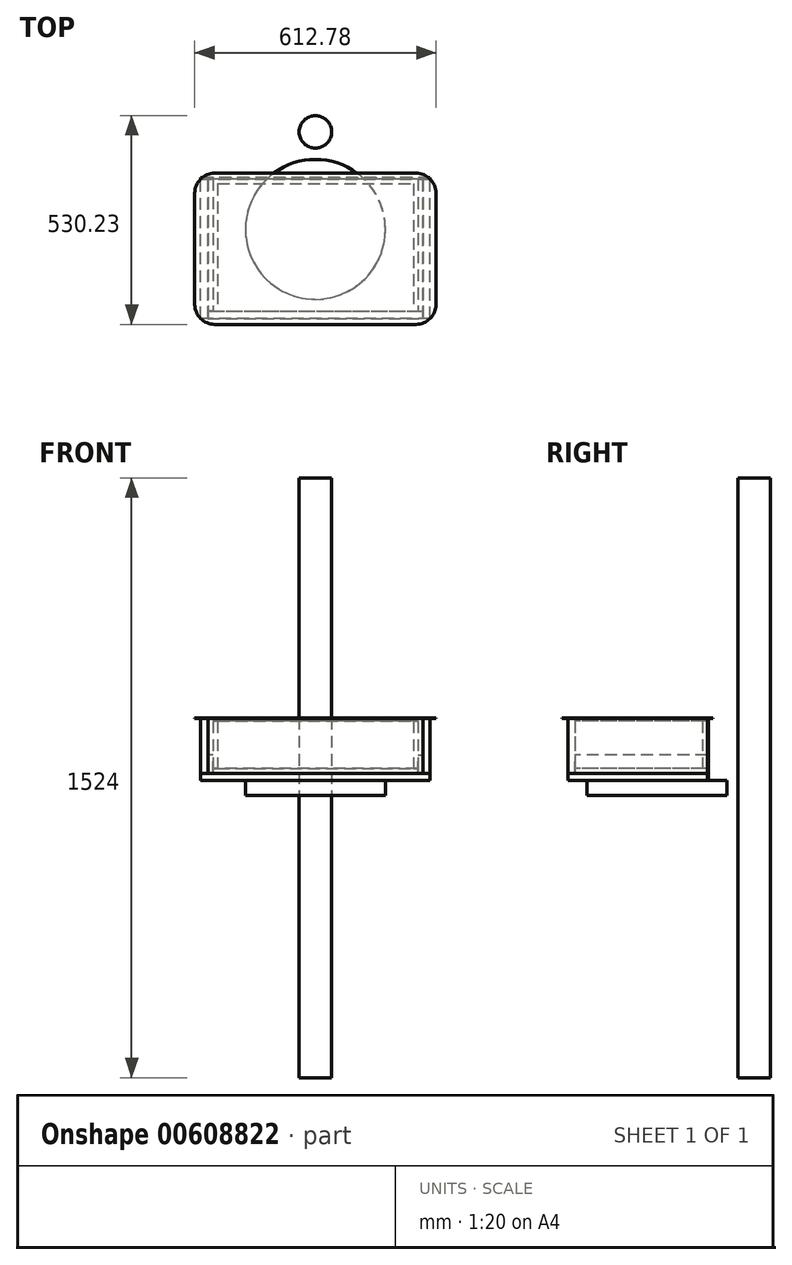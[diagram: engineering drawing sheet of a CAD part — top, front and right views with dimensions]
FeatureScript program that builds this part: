
annotation { "Feature Type Name" : "Feature", "Feature Type Description" : "" }
export const myFeature = defineFeature(function(context is Context, id is Id, definition is map)
    precondition{}
    {
        {
            var Q0;
            Q0=qCreatedBy(makeId("Top.planeOp"),FACE);
            var sketch = newSketch(context, id + "F0", { "sketchPlane" : qUnion([Q0])});
            skCircle(sketch, "E0", {"center": v(0, 0) * mm, "radius": 177.8 * mm});
            skSolve(sketch);
        }
        {
            var Q0;
            Q0 = qSketchRegion(id + "F0", true);
            extrude(context, id + "F1", {"entities" : qUnion([Q0]), "depth" : 38.1 * mm, "offsetDistance" : 25.4 * mm});
        }
        {
            var Q0;
            Q0=makeQuery(id+"F1.opExtrude","CAP_FACE",FACE,{"disambiguationData":[OSD([sQuery(id+"F0.wireOp",EDGE,"E0")])],"isStart":false});
            cPlane(context, id + "F2", {"entities" : qUnion([Q0]), "cplaneType" : CPlaneType.OFFSET, "offset" : 157.96 * mm, "width" : 152.4 * mm, "height" : 152.4 * mm});
        }
        {
            var Q0;
            Q0=qCreatedBy(id+"F2.planeOp",FACE);
            var sketch = newSketch(context, id + "F3", { "sketchPlane" : qUnion([Q0])});
            skLineSegment(sketch, "E1.bottom", {"start": v(255.59, -241.3) * mm, "end": v(-255.59, -241.3) * mm});
            skLineSegment(sketch, "E1.top", {"start": v(255.59, 142.88) * mm, "end": v(-255.59, 142.87) * mm});
            skLineSegment(sketch, "E1.left", {"start": v(306.39, -190.5) * mm, "end": v(306.39, 92.08) * mm});
            skLineSegment(sketch, "E1.right", {"start": v(-306.39, -190.5) * mm, "end": v(-306.39, 92.07) * mm});
            skPoint(sketch, "E2.visualSharp", {"position": v(-306.39, 142.87) * mm});
            skArc(sketch, "E2.filletArc", {"start": v(-255.59, 142.87) * mm, "mid": v(-291.5, 128) * mm, "end": v(-306.39, 92.07) * mm});
            skPoint(sketch, "E3.visualSharp", {"position": v(-306.39, -241.3) * mm});
            skArc(sketch, "E3.filletArc", {"start": v(-306.39, -190.5) * mm, "mid": v(-291.5, -226.42) * mm, "end": v(-255.59, -241.3) * mm});
            skPoint(sketch, "E4.visualSharp", {"position": v(306.39, -241.3) * mm});
            skArc(sketch, "E4.filletArc", {"start": v(255.59, -241.3) * mm, "mid": v(291.5, -226.42) * mm, "end": v(306.39, -190.5) * mm});
            skPoint(sketch, "E5.visualSharp", {"position": v(306.39, 142.88) * mm});
            skArc(sketch, "E5.filletArc", {"start": v(306.39, 92.08) * mm, "mid": v(291.5, 128) * mm, "end": v(255.59, 142.88) * mm});
            skLineSegment(sketch, "E6", {"start": v(0, 142.87) * mm, "end": v(0, -241.3) * mm, "construction": true});
            skSolve(sketch);
        }
        {
            var Q0;
            Q0 = qSketchRegion(id + "F3", true);
            extrude(context, id + "F4", {"entities" : qUnion([Q0]), "operationType" : NewBodyOperationType.ADD, "depth" : (1 + (3 / 8)) * mm, "offsetDistance" : 25.4 * mm});
        }
        {
            var Q0;
            Q0=makeQuery(id+"F1.opExtrude","CAP_FACE",FACE,{"disambiguationData":[OSD([sQuery(id+"F0.wireOp",EDGE,"E0")])],"isStart":false});
            var sketch = newSketch(context, id + "F5", { "sketchPlane" : qUnion([Q0])});
            skLineSegment(sketch, "E7.bottom", {"start": v(291.5, -226.42) * mm, "end": v(-291.5, -226.42) * mm});
            skLineSegment(sketch, "E7.top", {"start": v(291.5, 128) * mm, "end": v(-291.5, 128) * mm});
            skLineSegment(sketch, "E7.left", {"start": v(291.5, -226.42) * mm, "end": v(291.5, 128) * mm});
            skLineSegment(sketch, "E7.right", {"start": v(-291.5, -226.42) * mm, "end": v(-291.5, 128) * mm});
            skPoint(sketch, "E7.middle", {"position": v(0, 0) * mm});
            skSolve(sketch);
        }
        {
            var Q0;
            Q0 = qSketchRegion(id + "F5", true);
            extrude(context, id + "F6", {"entities" : qUnion([Q0]), "depth" : 18.26 * mm, "offsetDistance" : 25.4 * mm});
        }
        {
            var Q0;
            Q0=makeQuery(id+"F6.opExtrude","CAP_FACE",FACE,{"disambiguationData":[OSD([sQuery(id+"F5.wireOp",EDGE,"E7.bottom"),sQuery(id+"F5.wireOp",EDGE,"E7.top"),sQuery(id+"F5.wireOp",EDGE,"E7.left"),sQuery(id+"F5.wireOp",EDGE,"E7.right")])],"isStart":false});
            var sketch = newSketch(context, id + "F7", { "sketchPlane" : qUnion([Q0])});
            skLineSegment(sketch, "E8.0.0", {"start": v(-273.25, -226.42) * mm, "end": v(-273.25, 128) * mm});
            skLineSegment(sketch, "E8.0.2", {"start": v(-291.5, 128) * mm, "end": v(-291.5, -226.42) * mm});
            skLineSegment(sketch, "E9", {"start": v(-291.5, 128) * mm, "end": v(-273.25, 128) * mm});
            skLineSegment(sketch, "E10", {"start": v(-291.5, -226.42) * mm, "end": v(-273.25, -226.42) * mm});
            skLineSegment(sketch, "E11", {"start": v(0, 128) * mm, "end": v(0, -226.42) * mm, "construction": true});
            skLineSegment(sketch, "E12.MirrorCS", {"start": v(291.5, 128) * mm, "end": v(273.25, 128) * mm});
            skLineSegment(sketch, "E13.MirrorCS", {"start": v(291.5, -226.42) * mm, "end": v(273.25, -226.42) * mm});
            skLineSegment(sketch, "E14.MirrorCS", {"start": v(291.5, 128) * mm, "end": v(291.5, -226.42) * mm});
            skLineSegment(sketch, "E15.MirrorCS", {"start": v(273.25, -226.42) * mm, "end": v(273.25, 128) * mm});
            skSolve(sketch);
        }
        {
            var Q0;
            Q0 = qSketchRegion(id + "F7", true);
            var Q1;
            Q1=makeQuery(id+"F4.opExtrude","CAP_FACE",FACE,{"disambiguationData":[OSD([sQuery(id+"F3.wireOp",EDGE,"E1.bottom"),sQuery(id+"F3.wireOp",EDGE,"E1.top"),sQuery(id+"F3.wireOp",EDGE,"E1.left"),sQuery(id+"F3.wireOp",EDGE,"E1.right"),sQuery(id+"F3.wireOp",EDGE,"E2.filletArc"),sQuery(id+"F3.wireOp",EDGE,"E3.filletArc"),sQuery(id+"F3.wireOp",EDGE,"E4.filletArc"),sQuery(id+"F3.wireOp",EDGE,"E5.filletArc")])],"isStart":true});
            extrude(context, id + "F8", {"entities" : qUnion([Q0]), "endBound" : BoundingType.UP_TO_SURFACE, "depth" : 25.4 * mm, "endBoundEntityFace" : qUnion([Q1]), "offsetDistance" : 25.4 * mm});
        }
        {
            var Q0;
            Q0=makeQuery(id+"F6.opExtrude","SWEPT_FACE",FACE,{"disambiguationData":[OSD([sQuery(id+"F5.wireOp",EDGE,"E7.top")])]});
            var sketch = newSketch(context, id + "F9", { "sketchPlane" : qUnion([Q0])});
            skLineSegment(sketch, "E16", {"start": v(291.5, 196.06) * mm, "end": v(-291.5, 196.06) * mm});
            skLineSegment(sketch, "E17", {"start": v(-291.5, 196.06) * mm, "end": v(-291.5, 38.1) * mm});
            skLineSegment(sketch, "E18", {"start": v(-291.5, 38.1) * mm, "end": v(291.5, 38.1) * mm});
            skLineSegment(sketch, "E19", {"start": v(291.5, 38.1) * mm, "end": v(291.5, 196.06) * mm});
            skSolve(sketch);
        }
        {
            var Q0;
            Q0 = qSketchRegion(id + "F9", true);
            extrude(context, id + "F10", {"entities" : qUnion([Q0]), "depth" : 3.17 * mm, "offsetDistance" : 25.4 * mm});
        }
        {
            var Q0;
            Q0=makeQuery(id+"F4.opExtrude","CAP_FACE",FACE,{"disambiguationData":[OSD([sQuery(id+"F3.wireOp",EDGE,"E1.bottom"),sQuery(id+"F3.wireOp",EDGE,"E1.top"),sQuery(id+"F3.wireOp",EDGE,"E1.left"),sQuery(id+"F3.wireOp",EDGE,"E1.right"),sQuery(id+"F3.wireOp",EDGE,"E2.filletArc"),sQuery(id+"F3.wireOp",EDGE,"E3.filletArc"),sQuery(id+"F3.wireOp",EDGE,"E4.filletArc"),sQuery(id+"F3.wireOp",EDGE,"E5.filletArc")])],"isStart":false});
            var sketch = newSketch(context, id + "F11", { "sketchPlane" : qUnion([Q0])});
            skCircle(sketch, "E20", {"center": v(0, 247.65) * mm, "radius": 41.28 * mm});
            skSolve(sketch);
        }
        {
            var Q0;
            Q0 = qSketchRegion(id + "F11", true);
            extrude(context, id + "F12", {"entities" : qUnion([Q0]), "depth" : 609.6 * mm, "offsetDistance" : 25.4 * mm, "hasSecondDirection" : true, "secondDirectionOppositeDirection" : true, "secondDirectionDepth" : 914.4 * mm});
        }
        {
            var Q0;
            Q0=makeQuery(id+"F6.opExtrude","SWEPT_FACE",FACE,{"disambiguationData":[OSD([sQuery(id+"F5.wireOp",EDGE,"E7.bottom")])]});
            var sketch = newSketch(context, id + "F13", { "sketchPlane" : qUnion([Q0])});
            skLineSegment(sketch, "E21.0", {"start": v(-273.25, 196.06) * mm, "end": v(-273.25, 56.36) * mm});
            skLineSegment(sketch, "E22.0", {"start": v(273.25, 196.06) * mm, "end": v(273.25, 56.36) * mm});
            skLineSegment(sketch, "E23", {"start": v(-273.25, 196.06) * mm, "end": v(273.25, 196.06) * mm});
            skLineSegment(sketch, "E24", {"start": v(273.25, 56.36) * mm, "end": v(-273.25, 56.36) * mm});
            skSolve(sketch);
        }
        {
            var Q0;
            Q0 = qSketchRegion(id + "F13", true);
            extrude(context, id + "F14", {"entities" : qUnion([Q0]), "oppositeDirection" : true, "depth" : 18.26 * mm, "offsetDistance" : 25.4 * mm});
        }
        {
            var Q0;
            Q0=makeQuery(id+"F14.opExtrude","CAP_FACE",FACE,{"disambiguationData":[OSD([sQuery(id+"F13.wireOp",EDGE,"E21.0"),sQuery(id+"F13.wireOp",EDGE,"E22.0"),sQuery(id+"F13.wireOp",EDGE,"E23"),sQuery(id+"F13.wireOp",EDGE,"E24")])],"isStart":false});
            var sketch = newSketch(context, id + "F15", { "sketchPlane" : qUnion([Q0])});
            skLineSegment(sketch, "E25.bottom", {"start": v(260.55, 56.36) * mm, "end": v(273.25, 56.36) * mm});
            skLineSegment(sketch, "E25.top", {"start": v(260.55, 102.4) * mm, "end": v(273.25, 102.4) * mm});
            skLineSegment(sketch, "E25.left", {"start": v(260.55, 56.36) * mm, "end": v(260.55, 102.4) * mm});
            skLineSegment(sketch, "E25.right", {"start": v(273.25, 56.36) * mm, "end": v(273.25, 102.4) * mm});
            skLineSegment(sketch, "E26.MirrorCS", {"start": v(-260.55, 56.36) * mm, "end": v(-273.25, 56.36) * mm});
            skLineSegment(sketch, "E27.MirrorCS", {"start": v(-260.55, 102.4) * mm, "end": v(-273.25, 102.4) * mm});
            skLineSegment(sketch, "E28.MirrorCS", {"start": v(-260.55, 56.36) * mm, "end": v(-260.55, 102.4) * mm});
            skLineSegment(sketch, "E29.MirrorCS", {"start": v(-273.25, 56.36) * mm, "end": v(-273.25, 102.4) * mm});
            skSolve(sketch);
        }
        {
            var Q0;
            Q0 = qSketchRegion(id + "F15", true);
            var Q1;
            Q1=makeQuery(id+"F10.opExtrude","CAP_FACE",FACE,{"disambiguationData":[OSD([sQuery(id+"F9.wireOp",EDGE,"E16"),sQuery(id+"F9.wireOp",EDGE,"E17"),sQuery(id+"F9.wireOp",EDGE,"E18"),sQuery(id+"F9.wireOp",EDGE,"E19")])],"isStart":true});
            extrude(context, id + "F16", {"entities" : qUnion([Q0]), "endBound" : BoundingType.UP_TO_SURFACE, "depth" : 25.4 * mm, "endBoundEntityFace" : qUnion([Q1]), "offsetDistance" : 25.4 * mm});
        }
        {
            var Q0;
            Q0=makeQuery(id+"F6.opExtrude","CAP_FACE",FACE,{"disambiguationData":[OSD([sQuery(id+"F5.wireOp",EDGE,"E7.bottom"),sQuery(id+"F5.wireOp",EDGE,"E7.top"),sQuery(id+"F5.wireOp",EDGE,"E7.left"),sQuery(id+"F5.wireOp",EDGE,"E7.right")])],"isStart":false});
            var sketch = newSketch(context, id + "F17", { "sketchPlane" : qUnion([Q0])});
            skLineSegment(sketch, "E30.0", {"start": v(-260.55, 128) * mm, "end": v(-260.55, -208.16) * mm});
            skLineSegment(sketch, "E31.0", {"start": v(260.55, 128) * mm, "end": v(260.55, -208.16) * mm});
            skLineSegment(sketch, "E32", {"start": v(-260.55, -208.16) * mm, "end": v(260.55, -208.16) * mm});
            skLineSegment(sketch, "E33", {"start": v(260.55, 128) * mm, "end": v(-260.55, 128) * mm});
            skSolve(sketch);
        }
        {
            var Q0;
            Q0 = qSketchRegion(id + "F17", true);
            extrude(context, id + "F18", {"entities" : qUnion([Q0]), "depth" : 11.9 * mm, "offsetDistance" : 25.4 * mm});
        }
        {
            var Q0;
            Q0=makeQuery(id+"F18.opExtrude","CAP_FACE",FACE,{"disambiguationData":[OSD([sQuery(id+"F17.wireOp",EDGE,"E30.0"),sQuery(id+"F17.wireOp",EDGE,"E31.0"),sQuery(id+"F17.wireOp",EDGE,"E32"),sQuery(id+"F17.wireOp",EDGE,"E33")])],"isStart":false});
            var sketch = newSketch(context, id + "F19", { "sketchPlane" : qUnion([Q0])});
            skLineSegment(sketch, "E34.0", {"start": v(-260.55, 128) * mm, "end": v(-260.55, -208.16) * mm});
            skLineSegment(sketch, "E34.1", {"start": v(260.55, 128) * mm, "end": v(260.55, -208.16) * mm});
            skLineSegment(sketch, "E35", {"start": v(-260.55, 128) * mm, "end": v(260.55, 128) * mm});
            skLineSegment(sketch, "E36.0", {"start": v(248.65, 116.09) * mm, "end": v(248.65, -208.16) * mm});
            skLineSegment(sketch, "E36.1", {"start": v(-248.65, 116.09) * mm, "end": v(248.65, 116.09) * mm});
            skLineSegment(sketch, "E36.2", {"start": v(-248.65, 116.09) * mm, "end": v(-248.65, -208.16) * mm});
            skLineSegment(sketch, "E37", {"start": v(-260.55, -208.16) * mm, "end": v(-248.65, -208.16) * mm});
            skLineSegment(sketch, "E38", {"start": v(260.55, -208.16) * mm, "end": v(248.65, -208.16) * mm});
            skSolve(sketch);
        }
        {
            var Q0;
            Q0 = qSketchRegion(id + "F19", true);
            extrude(context, id + "F20", {"entities" : qUnion([Q0]), "depth" : 120.65 * mm, "offsetDistance" : 25.4 * mm});
        }
    });
